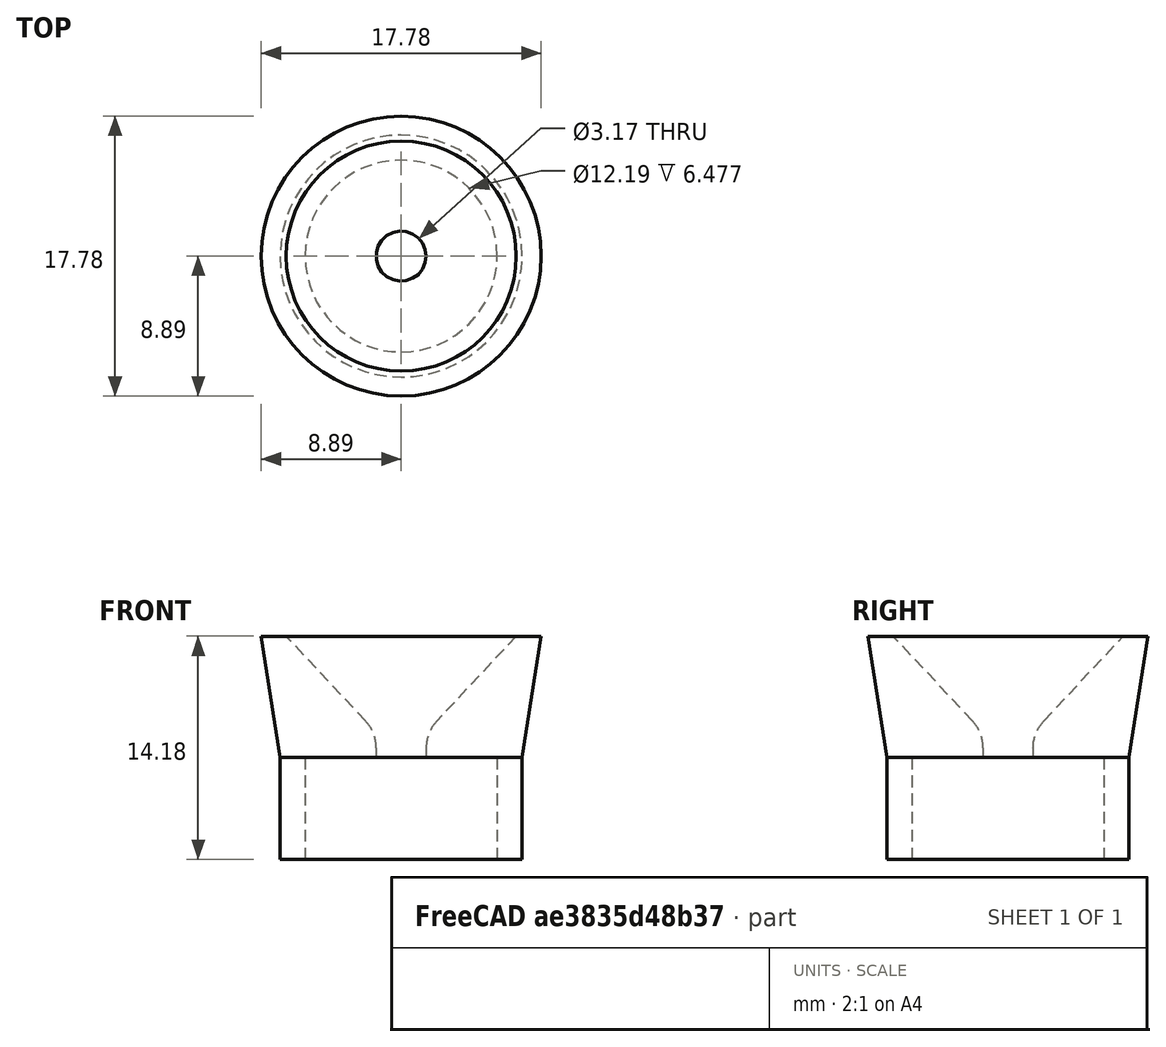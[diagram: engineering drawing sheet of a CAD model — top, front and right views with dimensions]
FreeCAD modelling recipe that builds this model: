
FCSTD DOCUMENT  (FreeCAD 0.19R24291 (Git))
Label: BuzzerHorn
License: All rights reserved
LicenseURL: http://en.wikipedia.org/wiki/All_rights_reserved
objects: TechDraw::DrawViewDimension×6, TechDraw::DrawProjGroupItem×4, TechDraw::DrawProjGroup×2, Sketcher::SketchObject×1, PartDesign::Revolution×1, TechDraw::DrawSVGTemplate×1, PartDesign::Fillet×1, PartDesign::Body×1, TechDraw::DrawViewAnnotation×1, TechDraw::DrawPage×1
note: 6 computed .brp shape members not serialized (recipe doc carries the construction recipe); baked Part::Feature solids carry a one-line shape summary decoded from their .brp

FEATURE [Sketcher::SketchObject] Sketch
  FullyConstrained = true
  MapMode = 5
  Placement = pos=(0,0,0) rot=(1,0,0;1.5708rad)
  Support = -> [XZ_Plane]
  sketch-geometry (8):
    g0: LineSegment StartX=6.096 StartY=0 StartZ=0 EndX=6.096 EndY=-6.477 EndZ=0
    g1: LineSegment StartX=6.096 StartY=-6.477 StartZ=0 EndX=7.6835 EndY=-6.477 EndZ=0
    g2: LineSegment StartX=7.6835 StartY=-6.477 StartZ=0 EndX=7.6835 EndY=0 EndZ=0
    g3: LineSegment StartX=7.6835 StartY=0 StartZ=0 EndX=8.89 EndY=7.6962 EndZ=0
    g4: LineSegment StartX=8.89 StartY=7.6962 StartZ=0 EndX=7.3025 EndY=7.6962 EndZ=0
    g5: LineSegment StartX=7.3025 StartY=7.6962 StartZ=0 EndX=1.5875 EndY=1.5875 EndZ=0
    g6: LineSegment StartX=1.5875 StartY=1.5875 StartZ=0 EndX=1.5875 EndY=0 EndZ=0
    g7: LineSegment StartX=1.5875 StartY=0 StartZ=0 EndX=6.096 EndY=0 EndZ=0
  constraints (24):
    c: PointOnObject(g0,g-1)
    c: Vertical(g0)
    c: Coincident(g0,g1)
    c: Horizontal(g1)
    c: Coincident(g1,g2)
    c: PointOnObject(g2,g-1)
    c: Vertical(g2)
    c: Coincident(g2,g3)
    c: Coincident(g3,g4)
    c: Horizontal(g4)
    c: Coincident(g4,g5)
    c: Coincident(g5,g6)
    c: Coincident(g6,g7)
    c: Coincident(g7,g0)
    c: Horizontal(g7)
    c: DistanceY(g0,g0) = 6.477
    c: DistanceX(g1,g1) = 1.5875
    c: DistanceX(g-1,g0) = 6.096
    c: Vertical(g6)
    c: DistanceX(g-1,g6) = 1.5875
    c: DistanceX(g4,g4) = 1.5875
    c: DistanceX(g-1,g4) = 7.3025
    c: DistanceY(g1,g4) = 14.1732
    c: DistanceY(g6,g5) = 1.5875
FEATURE [PartDesign::Revolution] Revolution
  Angle = 360
  Axis = (0,-2e-16,1)
  Base = (0,0,0)
  Placement = pos=(0,0,0) rot=(1,0,0;1.5708rad)
  Profile = -> Sketch
  ReferenceAxis = -> Sketch [V_Axis]
  Reversed = true
FEATURE [TechDraw::DrawSVGTemplate] Template
  Height = 215.9
  Orientation = 1
  Width = 279.4
FEATURE [PartDesign::Fillet] Fillet
  Base = -> Revolution [Edge10]
  BaseFeature = -> Revolution
  Placement = pos=(0,0,0) rot=(1,0,0;1.5708rad)
  Radius = 2.54
  SupportTransform = false
FEATURE [PartDesign::Body] Body
  Group = -> [Sketch,Revolution,Fillet]
  Origin = -> Origin
  Tip = -> Fillet
FEATURE [TechDraw::DrawProjGroupItem] ProjItem  label="Front"
  CoarseView = false
  Direction = (0,-1,0)
  Focus = 100
  HardHidden = false
  IsoCount = 0
  IsoHidden = false
  IsoVisible = false
  LockPosition = true
  Perspective = false
  Rotation = 0
  RotationVector = (1,0,0)
  Scale = 0.5
  ScaleType = 2
  SeamHidden = false
  SeamVisible = true
  SmoothHidden = false
  SmoothVisible = true
  Source = -> [Body]
  Type = 0
  X = 0
  XDirection = (1,0,0)
  Y = 0
FEATURE [TechDraw::DrawProjGroupItem] ProjItem001  label="Bottom"
  CoarseView = false
  Direction = (0,0,-1)
  Focus = 100
  HardHidden = false
  IsoCount = 0
  IsoHidden = false
  IsoVisible = false
  LockPosition = false
  Perspective = false
  Rotation = 0
  RotationVector = (1,0,0)
  Scale = 0.5
  ScaleType = 2
  SeamHidden = false
  SeamVisible = true
  SmoothHidden = false
  SmoothVisible = true
  Source = -> [Body]
  Type = 5
  X = 0
  XDirection = (1,0,0)
  Y = -23.9014
FEATURE [TechDraw::DrawProjGroupItem] ProjItem002  label="Left"
  CoarseView = false
  Direction = (-1,-1e-16,0)
  Focus = 100
  HardHidden = false
  IsoCount = 0
  IsoHidden = false
  IsoVisible = false
  LockPosition = false
  Perspective = false
  Rotation = 0
  RotationVector = (1,0,0)
  Scale = 0.5
  ScaleType = 2
  SeamHidden = false
  SeamVisible = true
  SmoothHidden = false
  SmoothVisible = true
  Source = -> [Body]
  Type = 1
  X = -23.9014
  XDirection = (1e-16,-1,0)
  Y = 0
FEATURE [TechDraw::DrawProjGroup] ProjGroup
  Anchor = -> ProjItem
  AutoDistribute = true
  LockPosition = false
  ProjectionType = 1
  Rotation = 0
  Scale = 0.5
  ScaleType = 2
  Source = -> [Body]
  Views = -> [ProjItem,ProjItem001,ProjItem002]
  X = 139.7
  Y = 107.95
  spacingX = 15.0114
  spacingY = 15.0114
FEATURE [TechDraw::DrawViewDimension] Dimension001
  Arbitrary = false
  ArbitraryTolerances = false
  EqualTolerance = true
  FormatSpec = %.3f
  FormatSpecOverTolerance = %+.3f
  FormatSpecUnderTolerance = %+.3f
  Inverted = false
  LockPosition = false
  MeasureType = 1
  OverTolerance = 0
  References2D = -> [ProjItem]
  Rotation = 0
  Scale = 0.5
  ScaleType = 2
  TheoreticalExact = false
  Type = 2
  UnderTolerance = 0
  X = 16.087
  Y = 15.0252
FEATURE [TechDraw::DrawViewDimension] Dimension002
  Arbitrary = false
  ArbitraryTolerances = false
  EqualTolerance = true
  FormatSpec = %.3f
  FormatSpecOverTolerance = %+.3f
  FormatSpecUnderTolerance = %+.3f
  Inverted = false
  LockPosition = false
  MeasureType = 1
  OverTolerance = 0
  References2D = -> [ProjItem]
  Rotation = 0
  Scale = 0.5
  ScaleType = 2
  TheoreticalExact = false
  Type = 2
  UnderTolerance = 0
  X = -13.7516
  Y = -1.68216
FEATURE [TechDraw::DrawViewDimension] Dimension003
  Arbitrary = false
  ArbitraryTolerances = false
  EqualTolerance = true
  FormatSpec = %.3f
  FormatSpecOverTolerance = %+.3f
  FormatSpecUnderTolerance = %+.3f
  Inverted = false
  LockPosition = false
  MeasureType = 1
  OverTolerance = 0
  References2D = -> [ProjItem002]
  Rotation = 0
  Scale = 0.5
  ScaleType = 2
  TheoreticalExact = false
  Type = 1
  UnderTolerance = 0
  X = 3.0548
  Y = 17.7626
FEATURE [TechDraw::DrawViewDimension] Dimension005
  Arbitrary = false
  ArbitraryTolerances = false
  EqualTolerance = true
  FormatSpec = %.3f
  FormatSpecOverTolerance = %+.3f
  FormatSpecUnderTolerance = %+.3f
  Inverted = false
  LockPosition = false
  MeasureType = 1
  OverTolerance = 0
  References2D = -> [ProjItem001]
  Rotation = 0
  Scale = 0.5
  ScaleType = 2
  TheoreticalExact = false
  Type = 1
  UnderTolerance = 0
  X = 7.96068
  Y = 14.7764
FEATURE [TechDraw::DrawViewAnnotation] Annotation
  Font = osifont
  LineSpace = 80
  LockPosition = false
  MaxWidth = -1
  Rotation = 0
  Scale = 0.5
  ScaleType = 2
  Text = Version 3.0 | Diamter about 0.6"
  TextSize = 5.0038
  TextStyle = 0
  X = 105.359
  Y = 151.83
FEATURE [TechDraw::DrawViewDimension] Dimension006
  Arbitrary = false
  ArbitraryTolerances = false
  EqualTolerance = true
  FormatSpec = %.3f
  FormatSpecOverTolerance = %+.3f
  FormatSpecUnderTolerance = %+.3f
  Inverted = false
  LockPosition = false
  MeasureType = 1
  OverTolerance = 0
  References2D = -> [ProjItem002]
  Rotation = 0
  Scale = 0.5
  ScaleType = 2
  TheoreticalExact = false
  Type = 2
  UnderTolerance = 0
  X = -14.5143
  Y = -2.47608
FEATURE [TechDraw::DrawViewDimension] Dimension007
  Arbitrary = false
  ArbitraryTolerances = false
  EqualTolerance = true
  FormatSpec = %.3f
  FormatSpecOverTolerance = %+.3f
  FormatSpecUnderTolerance = %+.3f
  Inverted = false
  LockPosition = false
  MeasureType = 1
  OverTolerance = 0
  References2D = -> [ProjItem002]
  Rotation = 0
  Scale = 0.5
  ScaleType = 2
  TheoreticalExact = false
  Type = 1
  UnderTolerance = 0
  X = 0.552027
  Y = -19.0001
FEATURE [TechDraw::DrawProjGroupItem] ProjItem003  label="Front001"
  CoarseView = false
  Direction = (0.439,-0.431,0.789)
  Focus = 100
  HardHidden = false
  IsoCount = 0
  IsoHidden = false
  IsoVisible = false
  LockPosition = true
  Perspective = false
  Rotation = 0
  RotationVector = (0.787,0.608,-0.106)
  Scale = 0.5
  ScaleType = 2
  SeamHidden = false
  SeamVisible = true
  SmoothHidden = false
  SmoothVisible = true
  Source = -> [Body]
  Type = 0
  X = 0
  XDirection = (0.787,0.608,-0.106)
  Y = 0
FEATURE [TechDraw::DrawProjGroup] ProjGroup001
  Anchor = -> ProjItem003
  AutoDistribute = true
  LockPosition = false
  ProjectionType = 0
  Rotation = 0
  Scale = 0.5
  ScaleType = 2
  Source = -> [Body]
  Views = -> [ProjItem003]
  X = 152.286
  Y = 150.346
  spacingX = 15.0114
  spacingY = 15.0114
FEATURE [TechDraw::DrawPage] Page
  KeepUpdated = true
  NextBalloonIndex = 1
  ProjectionType = 0
  Scale = 2
  Template = -> Template
  Views = -> [ProjGroup,Dimension001,Dimension002,Dimension003,Dimension005,Annotation,Dimension006,Dimension007,ProjGroup001]
